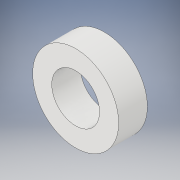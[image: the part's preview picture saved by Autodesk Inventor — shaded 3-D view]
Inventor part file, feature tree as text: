
AUTODESK INVENTOR PART (.ipt)
format: ipt  version: 2018 (Build 220112000, 112)  size: 99,328 bytes
history: native  units: in
note: dims shown in document units (in); Inventor stores cm internally (conversion verified against a paired STEP export)
features: extrude x1, sketch x1
ambient origin geometry x8: Origin, YZ Plane, XZ Plane, XY Plane, X Axis, Y Axis, Z Axis, Center Point
bodies: Solid1 (feature_tree)
feature tree (2):
  extrude  "Extrusion1"  Depth=0.1181in
  sketch  "Sketch1"  dims[d0=0.0787in d1=0.1969in d2=0.1181in d3=0.0in]
